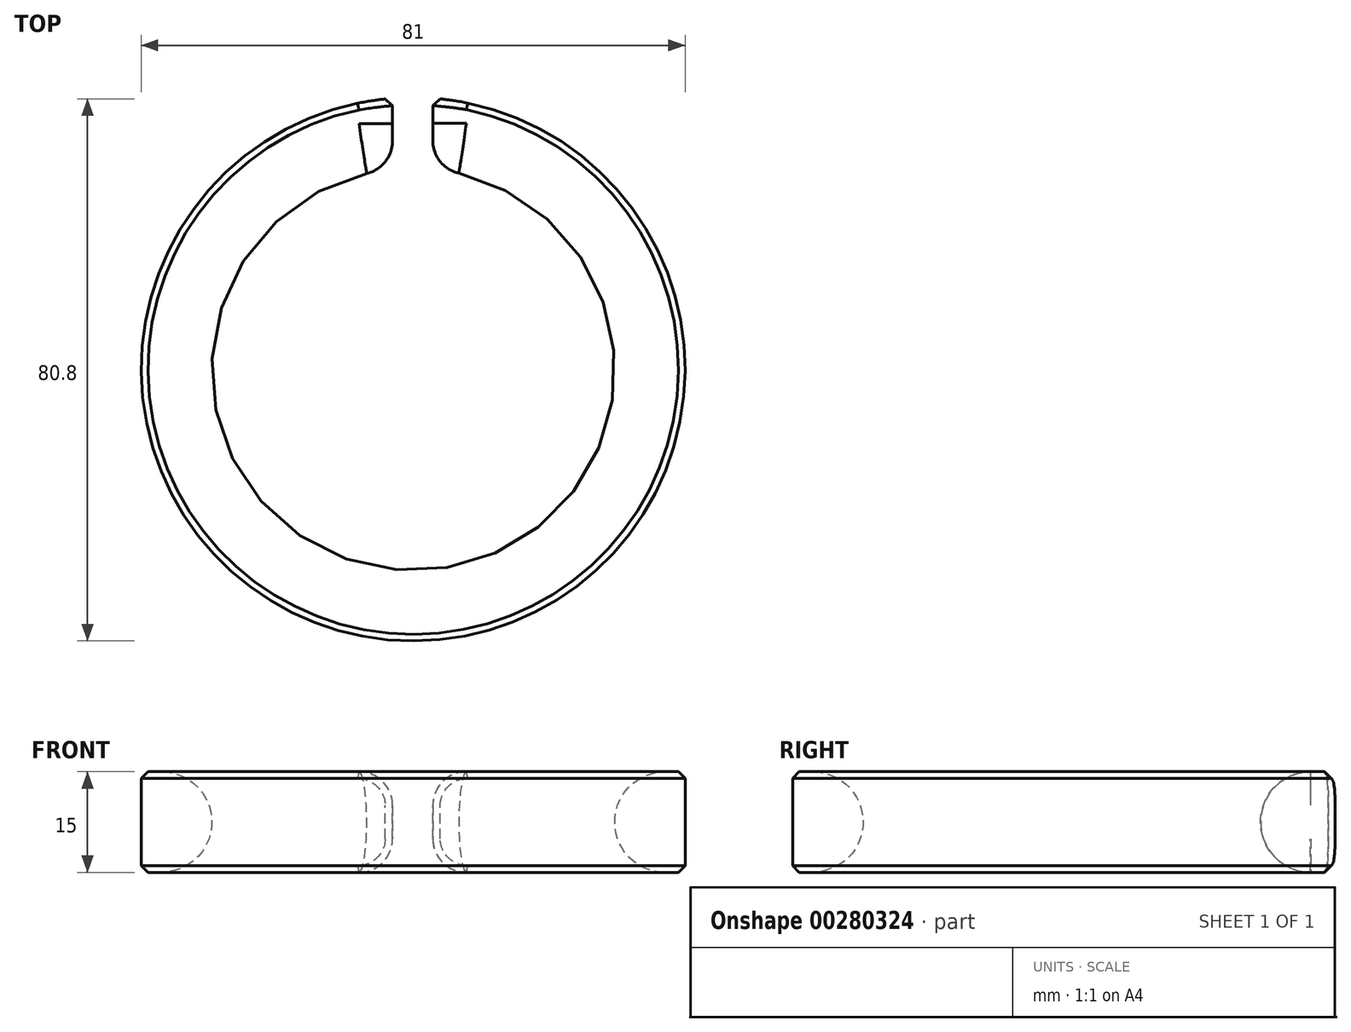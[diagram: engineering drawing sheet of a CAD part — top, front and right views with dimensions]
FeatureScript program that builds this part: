
annotation { "Feature Type Name" : "Feature", "Feature Type Description" : "" }
export const myFeature = defineFeature(function(context is Context, id is Id, definition is map)
    precondition{}
    {
        {
            var Q0;
            Q0=qCreatedBy(makeId("Front.planeOp"),FACE);
            var sketch = newSketch(context, id + "F0", { "sketchPlane" : qUnion([Q0])});
            skArc(sketch, "E0", {"start": v(-37.5, -7.5) * mm, "mid": v(-30, 0) * mm, "end": v(-37.5, 7.5) * mm});
            skLineSegment(sketch, "E1.bottom", {"start": v(-37.5, 7.5) * mm, "end": v(-40.5, 7.5) * mm});
            skLineSegment(sketch, "E1.top", {"start": v(-37.5, -7.5) * mm, "end": v(-40.5, -7.5) * mm});
            skLineSegment(sketch, "E1.right", {"start": v(-40.5, 7.5) * mm, "end": v(-40.5, -7.5) * mm});
            skSolve(sketch);
        }
        {
            var Q0;
            Q0=qCreatedBy(makeId("Front.planeOp"),FACE);
            var sketch = newSketch(context, id + "F1", { "sketchPlane" : qUnion([Q0])});
            skLineSegment(sketch, "E2", {"start": v(0, 35.6) * mm, "end": v(0, -36.07) * mm});
            skSolve(sketch);
        }
        {
            var Q0;
            Q0 = qSketchRegion(id + "F0", true);
            var Q1;
            Q1=sQuery(id+"F1.wireOp",EDGE,"E2");
            revolve(context, id + "F2", {"entities" : qUnion([Q0]), "axis" : qUnion([Q1]), "revolveType" : RevolveType.FULL});
        }
        {
            var Q0;
            Q0=qCreatedBy(makeId("Top.planeOp"),FACE);
            var sketch = newSketch(context, id + "F3", { "sketchPlane" : qUnion([Q0])});
            skLineSegment(sketch, "E3.bottom", {"start": v(-3.08, 56.16) * mm, "end": v(2.92, 56.16) * mm});
            skLineSegment(sketch, "E3.top", {"start": v(-3.08, 12.72) * mm, "end": v(2.92, 12.72) * mm});
            skLineSegment(sketch, "E3.left", {"start": v(-3.08, 56.16) * mm, "end": v(-3.08, 12.72) * mm});
            skLineSegment(sketch, "E3.right", {"start": v(2.92, 56.16) * mm, "end": v(2.92, 12.72) * mm});
            skSolve(sketch);
        }
        {
            var Q0;
            Q0 = qSketchRegion(id + "F3", true);
            extrude(context, id + "F4", {"entities" : qUnion([Q0]), "operationType" : NewBodyOperationType.REMOVE, "endBound" : BoundingType.SYMMETRIC, "oppositeDirection" : true, "depth" : 25 * mm});
        }
        {
            var Q0;
            Q0=makeQuery(id+"F4.boolean.opBoolean","INTERSECT",EDGE,{"derivedFrom":[makeQuery(id+"F2.opRevolve","SWEPT_FACE",FACE,{"disambiguationData":[OSD([sQuery(id+"F0.wireOp",EDGE,"E0")])]}),makeQuery(id+"F4.opExtrude","SWEPT_FACE",FACE,{"disambiguationData":[OSD([sQuery(id+"F3.wireOp",EDGE,"E3.left")])]})]});
            var Q1;
            Q1=makeQuery(id+"F4.boolean.opBoolean","INTERSECT",EDGE,{"derivedFrom":[makeQuery(id+"F2.opRevolve","SWEPT_FACE",FACE,{"disambiguationData":[OSD([sQuery(id+"F0.wireOp",EDGE,"E0")])]}),makeQuery(id+"F4.opExtrude","SWEPT_FACE",FACE,{"disambiguationData":[OSD([sQuery(id+"F3.wireOp",EDGE,"E3.right")])]})]});
            fillet(context, id + "F5", {"entities" : qUnion([Q0, Q1]), "radius" : 5 * mm, "tangentPropagation" : true, "allowEdgeOverflow" : false});
        }
        {
            var Q0;
            Q0=makeQuery(id+"F2.opRevolve","SWEPT_EDGE",EDGE,{"disambiguationData":[OSD([sQuery(id+"F0.wireOp",EDGE,"E1.top"),sQuery(id+"F0.wireOp",EDGE,"E1.right")])]});
            chamfer(context, id + "F6", {"entities" : qUnion([Q0]), "width" : 1 * mm, "tangentPropagation" : true});
        }
    });
